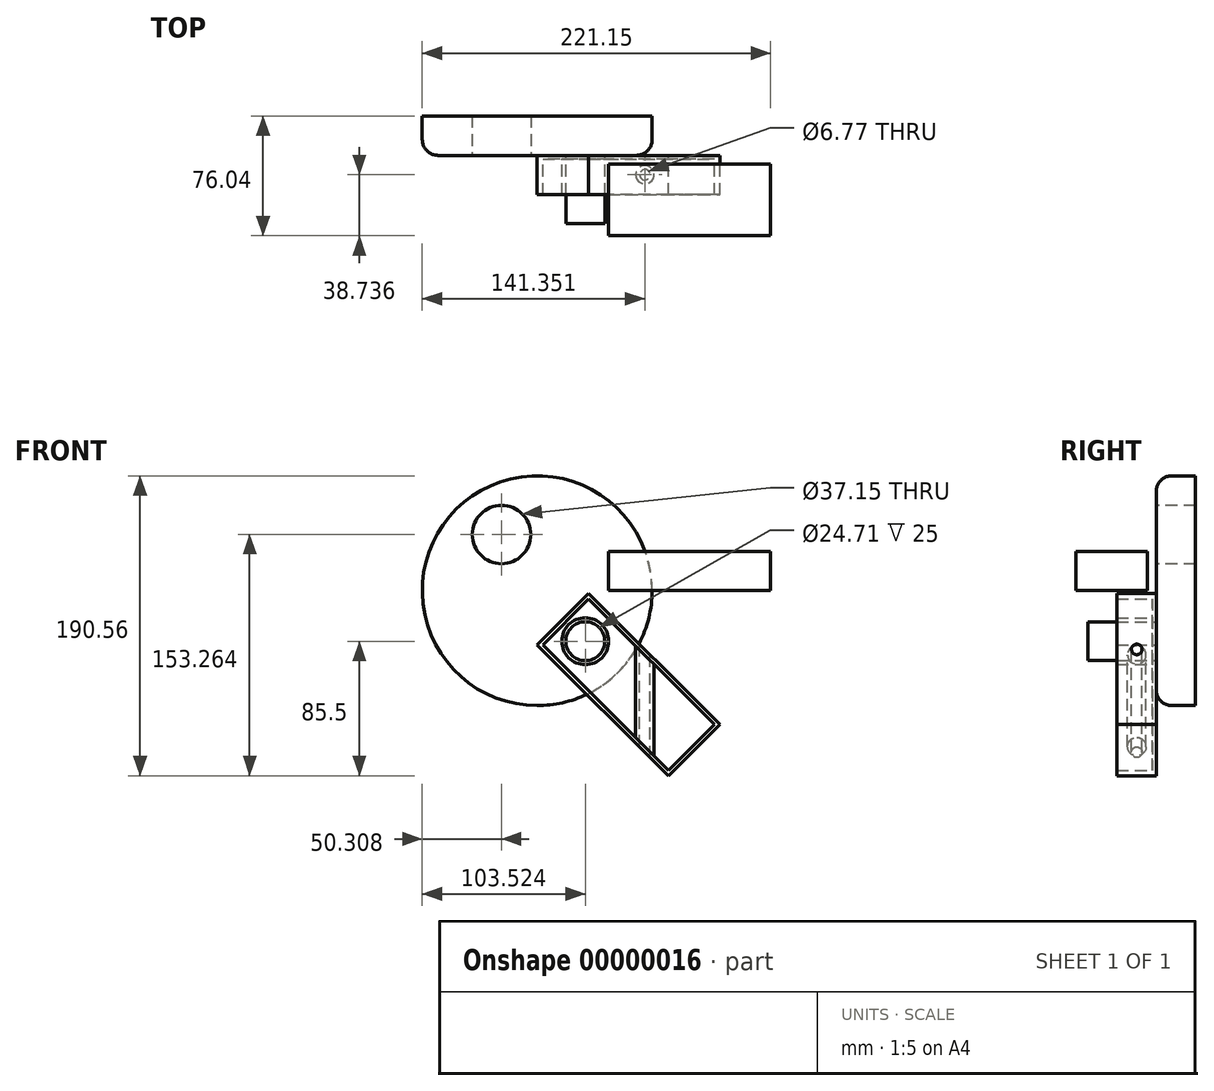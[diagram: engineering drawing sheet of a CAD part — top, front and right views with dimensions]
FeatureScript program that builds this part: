
annotation { "Feature Type Name" : "Feature", "Feature Type Description" : "" }
export const myFeature = defineFeature(function(context is Context, id is Id, definition is map)
    precondition{}
    {
        {
            var Q0;
            Q0=qCreatedBy(makeId("Front.planeOp"),FACE);
            var sketch = newSketch(context, id + "F0", { "sketchPlane" : qUnion([Q0])});
            skCircle(sketch, "E0", {"center": v(0, 0) * mm, "radius": 72.97 * mm});
            skSolve(sketch);
        }
        {
            var Q0;
            Q0=makeQuery(id+"F0.imprint","IMPRINT",FACE,{"disambiguationData":[TD([[makeQuery(id+"F0.imprint","IMPRINT",EDGE,{"derivedFrom":sQuery(id+"F0.wireOp",EDGE,"E0")}),1.0]])]});
            extrude(context, id + "F1", {"entities" : qUnion([Q0]), "depth" : 25 * mm});
        }
        {
            var Q0;
            Q0=makeQuery(id+"F1.opExtrude","CAP_EDGE",EDGE,{"disambiguationData":[OSD([sQuery(id+"F0.wireOp",EDGE,"E0")])],"isStart":false});
            fillet(context, id + "F2", {"entities" : qUnion([Q0]), "radius" : 10 * mm, "tangentPropagation" : true, "allowEdgeOverflow" : false});
        }
        {
            var Q0;
            Q0=makeQuery(id+"F1.opExtrude","CAP_FACE",FACE,{"disambiguationData":[OSD([sQuery(id+"F0.wireOp",EDGE,"E0")])],"isStart":false});
            var sketch = newSketch(context, id + "F3", { "sketchPlane" : qUnion([Q0])});
            skCircle(sketch, "E1", {"center": v(-22.66, 35.67) * mm, "radius": 18.57 * mm});
            skSolve(sketch);
        }
        {
            var Q0;
            Q0=makeQuery(id+"F3.imprint","IMPRINT",FACE,{"disambiguationData":[TD([[makeQuery(id+"F3.imprint","IMPRINT",EDGE,{"derivedFrom":sQuery(id+"F3.wireOp",EDGE,"E1")}),1.0]])]});
            extrude(context, id + "F4", {"entities" : qUnion([Q0]), "operationType" : NewBodyOperationType.REMOVE, "endBound" : BoundingType.THROUGH_ALL, "oppositeDirection" : true, "depth" : 25 * mm});
        }
        {
            var Q0;
            Q0=makeQuery(id+"F1.opExtrude","CAP_FACE",FACE,{"disambiguationData":[OSD([sQuery(id+"F0.wireOp",EDGE,"E0")])],"isStart":false});
            var sketch = newSketch(context, id + "F5", { "sketchPlane" : qUnion([Q0])});
            skCircle(sketch, "E2", {"center": v(30.55, -32.1) * mm, "radius": 12.36 * mm});
            skSolve(sketch);
        }
        {
            var Q0;
            Q0=makeQuery(id+"F5.imprint","IMPRINT",FACE,{"disambiguationData":[TD([[makeQuery(id+"F5.imprint","IMPRINT",EDGE,{"derivedFrom":sQuery(id+"F5.wireOp",EDGE,"E2")}),1.0]])]});
            extrude(context, id + "F6", {"entities" : qUnion([Q0]), "operationType" : NewBodyOperationType.ADD, "depth" : 43.47 * mm});
        }
        {
            var Q0;
            Q0=makeQuery(id+"F1.opExtrude","CAP_FACE",FACE,{"disambiguationData":[OSD([sQuery(id+"F0.wireOp",EDGE,"E0")])],"isStart":false});
            var sketch = newSketch(context, id + "F7", { "sketchPlane" : qUnion([Q0])});
            skLineSegment(sketch, "E3", {"start": v(32.66, -1.68) * mm, "end": v(116.03, -84.85) * mm});
            skLineSegment(sketch, "E4", {"start": v(116.03, -84.85) * mm, "end": v(83.38, -117.6) * mm});
            skLineSegment(sketch, "E5", {"start": v(83.38, -117.6) * mm, "end": v(0, -34.42) * mm});
            skLineSegment(sketch, "E6", {"start": v(0, -34.42) * mm, "end": v(32.66, -1.68) * mm});
            skSolve(sketch);
        }
        {
            var Q0;
            {var subQ6=sQuery(id+"F7.wireOp",EDGE,"E4");Q0=makeQuery(id+"F7.imprint","IMPRINT",FACE,{"disambiguationData":[TD([[makeQuery(id+"F7.imprint","IMPRINT",EDGE,{"derivedFrom":subQ6}),-1.0]])]});}
            var Q1;
            {var subQ6=sQuery(id+"F7.wireOp",EDGE,"E6");Q1=makeQuery(id+"F7.imprint","IMPRINT",FACE,{"disambiguationData":[TD([[makeQuery(id+"F7.imprint","IMPRINT",EDGE,{"derivedFrom":subQ6}),-1.0]])]});}
            extrude(context, id + "F8", {"entities" : qUnion([Q0, Q1]), "depth" : 25 * mm});
        }
        {
            var Q0;
            Q0=qCreatedBy(makeId("Top.planeOp"),FACE);
            var sketch = newSketch(context, id + "F9", { "sketchPlane" : qUnion([Q0])});
            skLineSegment(sketch, "E7.bottom", {"start": v(45.13, -30.42) * mm, "end": v(148.18, -30.42) * mm});
            skLineSegment(sketch, "E7.top", {"start": v(45.13, -76.04) * mm, "end": v(148.18, -76.04) * mm});
            skLineSegment(sketch, "E7.left", {"start": v(45.13, -30.42) * mm, "end": v(45.13, -76.04) * mm});
            skLineSegment(sketch, "E7.right", {"start": v(148.18, -30.42) * mm, "end": v(148.18, -76.04) * mm});
            skSolve(sketch);
        }
        {
            var Q0;
            Q0=makeQuery(id+"F9.imprint","IMPRINT",FACE,{"disambiguationData":[TD([[makeQuery(id+"F9.imprint","IMPRINT",EDGE,{"derivedFrom":sQuery(id+"F9.wireOp",EDGE,"E7.bottom")}),-1.0]])]});
            extrude(context, id + "F10", {"entities" : qUnion([Q0]), "depth" : 25 * mm});
        }
        {
            var Q0;
            Q0=makeQuery(id+"F10.opExtrude","CAP_FACE",FACE,{"disambiguationData":[OSD([sQuery(id+"F9.wireOp",EDGE,"E7.bottom"),sQuery(id+"F9.wireOp",EDGE,"E7.top"),sQuery(id+"F9.wireOp",EDGE,"E7.left"),sQuery(id+"F9.wireOp",EDGE,"E7.right")])],"isStart":true});
            var sketch = newSketch(context, id + "F11", { "sketchPlane" : qUnion([Q0])});
            skCircle(sketch, "E8", {"center": v(68.38, 37.3) * mm, "radius": 3.39 * mm});
            skSolve(sketch);
        }
        {
            var Q0;
            Q0=makeQuery(id+"F11.imprint","IMPRINT",FACE,{"disambiguationData":[TD([[makeQuery(id+"F11.imprint","IMPRINT",EDGE,{"derivedFrom":sQuery(id+"F11.wireOp",EDGE,"E8")}),1.0]])]});
            extrude(context, id + "F12", {"entities" : qUnion([Q0]), "operationType" : NewBodyOperationType.REMOVE, "endBound" : BoundingType.THROUGH_ALL, "depth" : 25 * mm});
        }
        {
            var Q0;
            Q0=makeQuery(id+"F8.opExtrude","CAP_FACE",FACE,{"disambiguationData":[OSD([sQuery(id+"F5.wireOp",EDGE,"E2"),sQuery(id+"F7.wireOp",EDGE,"E3"),sQuery(id+"F7.wireOp",EDGE,"E4"),sQuery(id+"F7.wireOp",EDGE,"E5"),sQuery(id+"F7.wireOp",EDGE,"E6")])],"isStart":false});
            shell(context, id + "F13", {"entities" : qUnion([Q0]), "thickness" : 2.5 * mm});
        }
    });
